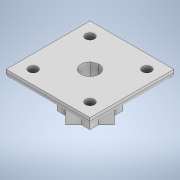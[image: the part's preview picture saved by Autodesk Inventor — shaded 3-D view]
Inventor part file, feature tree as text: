
AUTODESK INVENTOR PART (.ipt)
format: ipt  version: 2021 (Build 250183000, 183)  size: 161,792 bytes
history: native  units: mm
features: extrude x4, sketch x4, other x1, fillet x1
ambient origin geometry x8: Origin, YZ Plane, XZ Plane, XY Plane, X Axis, Y Axis, Z Axis, Center Point
bodies: Body1 (feature_tree)
feature tree (10):
  other  "Sólido1"
  extrude  "Extrusión1"  Depth=9.0mm TaperAngle=0.0deg
  extrude  "Extrusión2"  Depth=4.5mm
  extrude  "Extrusión5"  Depth=3.0mm TaperAngle=360.0deg
  fillet  "Empalme1"  Radius=6.0mm
  extrude  "Extrusión7"  Depth=2.0mm
  sketch  "Boceto1"  dims[d11=2.744mm d16=9.0mm d17=0.0mm]
  sketch  "Boceto2"  dims[d22=3.0mm d23=0.0mm d26=4.5mm]
  sketch  "Boceto5"  dims[d28=3.0mm d29=40.0mm d31=360.0deg d48=6.0mm]
  sketch  "Boceto7"  dims[d50=100.0mm d51=0.0mm d52=2.0mm d75=3.0mm d76=40.0mm d78=360.0deg d80=190.0mm d81=0.0mm d18=0.5mm d19=0.872665mm]
